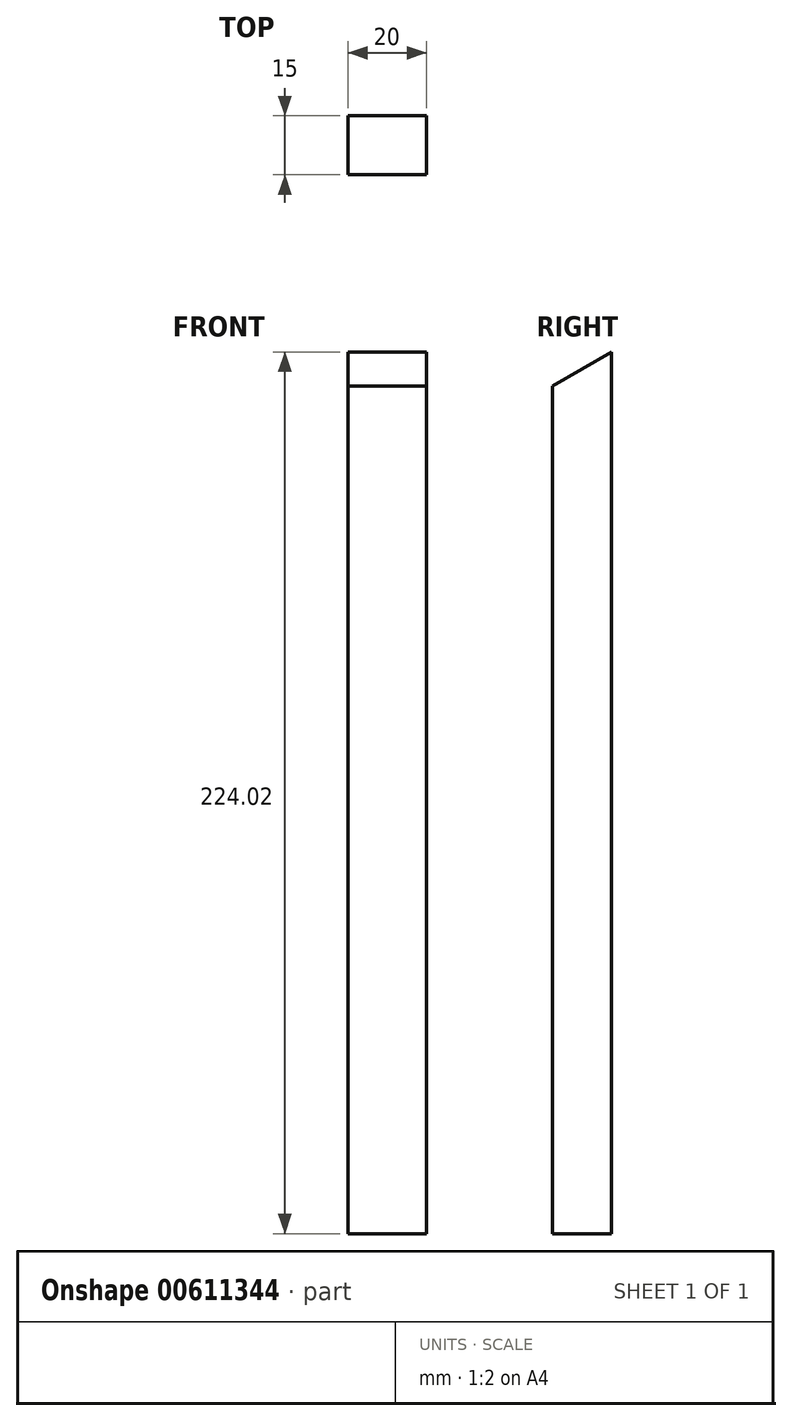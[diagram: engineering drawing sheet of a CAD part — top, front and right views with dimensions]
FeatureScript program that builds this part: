
annotation { "Feature Type Name" : "Feature", "Feature Type Description" : "" }
export const myFeature = defineFeature(function(context is Context, id is Id, definition is map)
    precondition{}
    {
        {
            var Q0;
            Q0=qCreatedBy(makeId("Front.planeOp"),FACE);
            var sketch = newSketch(context, id + "F0", { "sketchPlane" : qUnion([Q0])});
            skLineSegment(sketch, "E0.bottom", {"start": v(-10, -112) * mm, "end": v(10, -112) * mm});
            skLineSegment(sketch, "E0.top", {"start": v(-10, 112) * mm, "end": v(10, 112) * mm});
            skLineSegment(sketch, "E0.left", {"start": v(-10, -112) * mm, "end": v(-10, 112) * mm});
            skLineSegment(sketch, "E0.right", {"start": v(10, -112) * mm, "end": v(10, 112) * mm});
            skPoint(sketch, "E0.middle", {"position": v(0, 0) * mm});
            skSolve(sketch);
        }
        {
            var Q0;
            Q0=makeQuery(id+"F0.imprint","IMPRINT",FACE,{"disambiguationData":[TD([[makeQuery(id+"F0.imprint","IMPRINT",EDGE,{"derivedFrom":sQuery(id+"F0.wireOp",EDGE,"E0.bottom")}),1.0]])]});
            extrude(context, id + "F1", {"entities" : qUnion([Q0]), "depth" : 15 * mm, "offsetDistance" : 25 * mm});
        }
        {
            var Q0;
            Q0=makeQuery(id+"F1.opExtrude","SWEPT_FACE",FACE,{"disambiguationData":[OSD([sQuery(id+"F0.wireOp",EDGE,"E0.left")])]});
            var sketch = newSketch(context, id + "F2", { "sketchPlane" : qUnion([Q0])});
            skLineSegment(sketch, "E1", {"start": v(0, 112) * mm, "end": v(15, 103.35) * mm});
            skLineSegment(sketch, "E2", {"start": v(15, 103.35) * mm, "end": v(15, 103.35) * mm});
            skLineSegment(sketch, "E3", {"start": v(15, 112) * mm, "end": v(15, 103.35) * mm});
            skLineSegment(sketch, "E4", {"start": v(15, 112) * mm, "end": v(0, 112) * mm});
            skSolve(sketch);
        }
        {
            var Q0;
            Q0=makeQuery(id+"F2.imprint","IMPRINT",FACE,{"disambiguationData":[TD([[makeQuery(id+"F2.imprint","IMPRINT",EDGE,{"derivedFrom":sQuery(id+"F2.wireOp",EDGE,"E1")}),1.0]])]});
            extrude(context, id + "F3", {"entities" : qUnion([Q0]), "operationType" : NewBodyOperationType.REMOVE, "endBound" : BoundingType.THROUGH_ALL, "oppositeDirection" : true, "depth" : 25 * mm, "offsetDistance" : 25 * mm});
        }
    });
